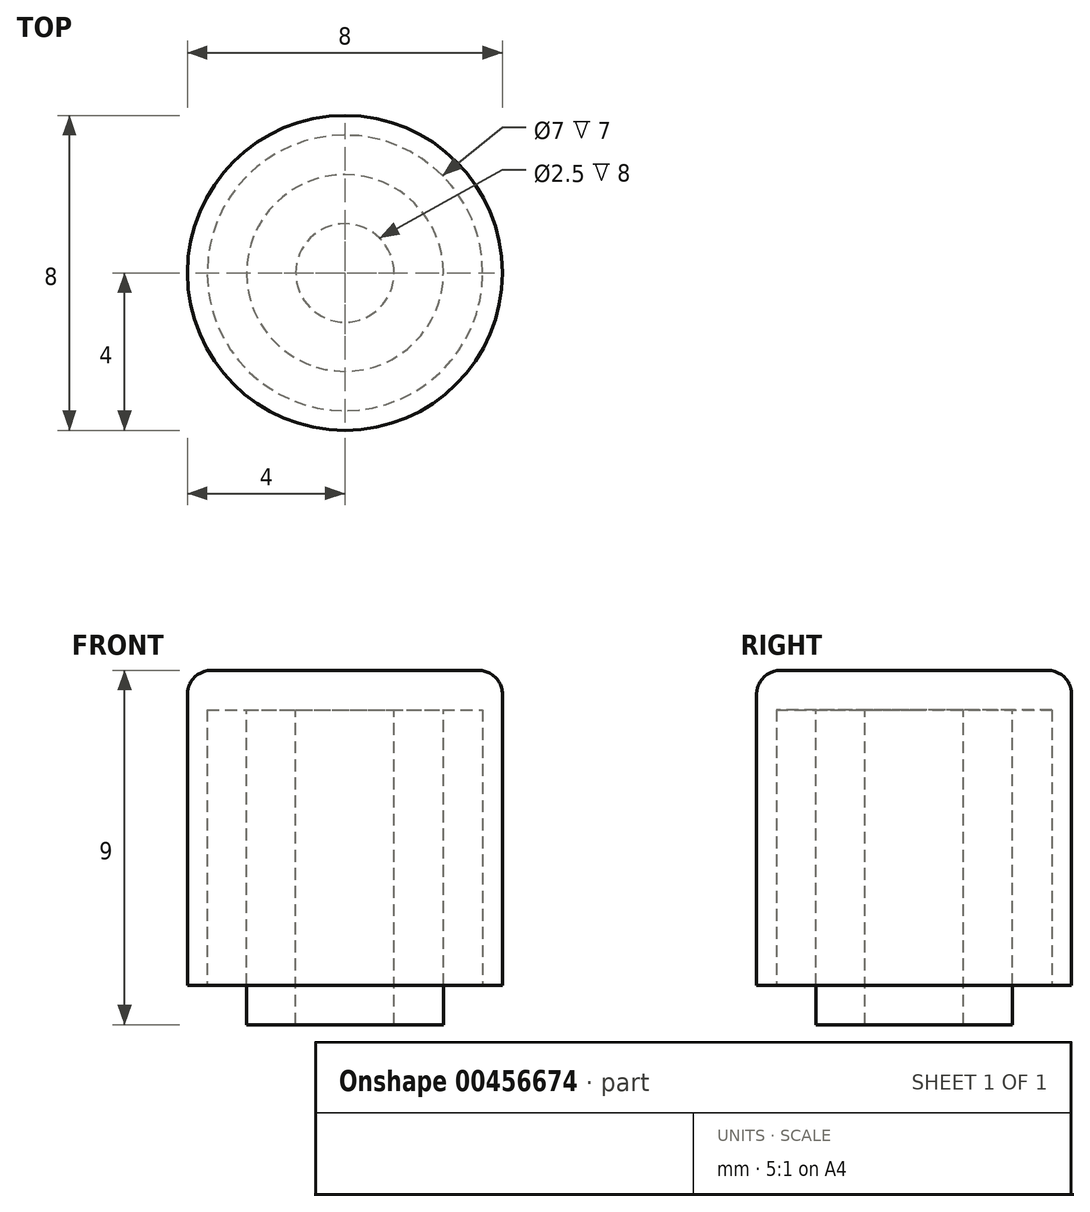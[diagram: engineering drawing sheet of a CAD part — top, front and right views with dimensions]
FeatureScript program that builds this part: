
annotation { "Feature Type Name" : "Feature", "Feature Type Description" : "" }
export const myFeature = defineFeature(function(context is Context, id is Id, definition is map)
    precondition{}
    {
        {
            var Q0;
            Q0=qCreatedBy(makeId("Top.planeOp"),FACE);
            var sketch = newSketch(context, id + "F0", { "sketchPlane" : qUnion([Q0])});
            skCircle(sketch, "E0", {"center": v(0, 0) * mm, "radius": 4 * mm});
            skSolve(sketch);
        }
        {
            var Q0;
            Q0 = qSketchRegion(id + "F0", true);
            extrude(context, id + "F1", {"entities" : qUnion([Q0]), "depth" : 8 * mm});
        }
        {
            var Q0;
            Q0=makeQuery(id+"F1.opExtrude","CAP_EDGE",EDGE,{"disambiguationData":[OSD([sQuery(id+"F0.wireOp",EDGE,"E0")])],"isStart":false});
            fillet(context, id + "F2", {"entities" : qUnion([Q0]), "radius" : 0.6 * mm, "tangentPropagation" : true, "allowEdgeOverflow" : false});
        }
        {
            var Q0;
            Q0=makeQuery(id+"F1.opExtrude","CAP_FACE",FACE,{"disambiguationData":[OSD([sQuery(id+"F0.wireOp",EDGE,"E0")])],"isStart":true});
            var sketch = newSketch(context, id + "F3", { "sketchPlane" : qUnion([Q0])});
            skCircle(sketch, "E1", {"center": v(0, 0) * mm, "radius": 3.5 * mm});
            skSolve(sketch);
        }
        {
            var Q0;
            Q0=makeQuery(id+"F3.imprint","IMPRINT",FACE,{"disambiguationData":[TD([[makeQuery(id+"F3.imprint","IMPRINT",EDGE,{"derivedFrom":sQuery(id+"F3.wireOp",EDGE,"E1")}),1.0]])]});
            extrude(context, id + "F4", {"entities" : qUnion([Q0]), "operationType" : NewBodyOperationType.REMOVE, "oppositeDirection" : true, "depth" : 7 * mm});
        }
        {
            var Q0;
            Q0=makeQuery(id+"F4.boolean.opBoolean","COPY",FACE,{"derivedFrom":makeQuery(id+"F4.opExtrude","CAP_FACE",FACE,{"disambiguationData":[OSD([sQuery(id+"F3.wireOp",EDGE,"E1")])],"isStart":false})});
            var sketch = newSketch(context, id + "F5", { "sketchPlane" : qUnion([Q0])});
            skCircle(sketch, "E2", {"center": v(0, 0) * mm, "radius": 2.5 * mm});
            skCircle(sketch, "E3", {"center": v(0, 0) * mm, "radius": 1.25 * mm});
            skSolve(sketch);
        }
        {
            var Q0;
            Q0=makeQuery(id+"F5.imprint","IMPRINT",FACE,{"disambiguationData":[TD([[makeQuery(id+"F5.imprint","IMPRINT",EDGE,{"derivedFrom":sQuery(id+"F5.wireOp",EDGE,"E2")}),1.0]])]});
            extrude(context, id + "F6", {"entities" : qUnion([Q0]), "operationType" : NewBodyOperationType.ADD, "depth" : 8 * mm});
        }
    });
